# Revit family: Bright 3.H
name_source: partatom
category: Lighting Fixtures
units: mm (PartAtom-declared; Revit-internal decimal feet)

## family parameters
Cut with Voids When Loaded = Yes
Host = Face
Light Source = Yes
Part Type = Normal
Room Calculation Point = Yes
Round Connector Dimension = Use Diameter
Shared = No

## types (3) — shared parameters
Apparent Load = 0 VA
Apparent Load Phase 1 = 11 W
Body = L&L_Anodized aluminium
CRI = -
Code = -
Color Filter = 16777215
Control system = -
Cutout dimensions = diam. 96 mm
Default Elevation = 1219 mm
Delivered lumen output = 278 lm, R: 43 lm G: 87 lm B: 32 lm W: 116 lm (4000K, 18°)
Description = recessed for outdoor applications
Dimming Lamp Color Temperature Shift = <None>
Emit from Line Length = 610 mm
Energy efficiency class = A A+ A++
Features = -
Geometry = Bright 3.H_mod
Height Void = 80 mm  [stored 0.262467 ft]
Height mm = 75 mm
IP = IP68, IP69K
LED Colour = RGBW
Length mm = 112 mm  [stored 0.367454 ft]
Lens = L&L_Tempered extra-clear glass
Lumen output at source = 447 lm, R: 68 lm G: 139 lm B: 51 lm W: 189 lm (4000K)
Manufacturer = L&L Luce&Light
Material = body in black-anodized anticorodal aluminium, trim in AISI 316L stainless steel, screen in tempered, serigraphed-grey and transparent extra-clear glass
Model = Bright 3.H
Mounting = recessed (ceiling, wall, floor)
No. and type of led = 1 RGBW power LED group, 50 000h L85 B10 (Ta 25°C)
Notes = -
Power = 11W
Power Supply = L&L_Steel inox AISI 316L
Power cables = includes 1.50 m FEP+RUB cable (equivalent to H05RN-F) 6x0.50/0.50 Ø6.3 mm
Power supply = 24Vdc
Power supply unit = not included
Radius Void = 50 mm  [stored 0.164042 ft]
Tilt Angle = 90.00°
Tiltable = -
Trim = L&L_Steel inox AISI 316L
URL = https://www.lucelight.it
URL Accessories and power supply units = https://www.lucelight.it
URL Catalogue = https://www.lucelight.it
URL DXF = https://www.lucelight.it
URL Description = https://www.lucelight.it
URL General code = https://www.lucelight.it
URL IES Photometric file = https://www.lucelight.it
URL Image = https://www.lucelight.it
URL Technical sheet = https://www.lucelight.it
Voltage = 24 V
Weight kg = 0.80 kg
Width mm = 112 mm  [stored 0.367454 ft]
Wiring = parallel

## per-type parameters (varying)
| type | Optics | Photometric Web File |
| Bright 3.H L 58° (RGBW 11W 24Vdc) | 58° | BRIGHT 3.H L 58° [RGBW 11W 24Vdc].IES |
| Bright 3.H M 32° (RGBW 11W 24Vdc) | 32° | BRIGHT 3.H M 32° [RGBW 11W 24Vdc].IES |
| Bright 3.H S 18° (RGBW 11W 24Vdc) | 18° | BRIGHT 3.H S 18° [RGBW 11W 24Vdc].IES |

note: [stored X ft] marks values corroborated as IEEE doubles in the binary element streams (Revit-internal decimal feet)

## geometry (parser evidence)
native form markers: Blend x2, Sweep x4
no freeform markers — native parametric forms only
